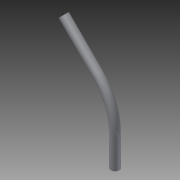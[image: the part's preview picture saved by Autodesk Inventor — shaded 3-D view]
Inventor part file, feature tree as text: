
AUTODESK INVENTOR PART (.ipt)
format: ipt  version: 2014 SP1 (Build 180222100, 222)  size: 118,784 bytes
history: native  units: in
note: dims shown in document units (in); Inventor stores cm internally (conversion verified against a paired STEP export)
features: reference x5, sketch x2, plane x1, sweep x1
ambient origin geometry x8: Origin, YZ Plane, XZ Plane, XY Plane, X Axis, Y Axis, Z Axis, Center Point
bodies: Solid1 (feature_tree)
feature tree (9):
  sketch  "Sketch1"  dims[d0=0.7274in d1=0.5in]
  plane  "Work Plane1"
  sweep  "Sweep1"
  reference  "Reference1"
  reference  "Reference2"
  reference  "Reference3"
  reference  "Reference4"
  sketch  "Sketch2"  dims[d2=0.7274in d3=0.0in d4=0.45in]
  reference  "Reference5"
